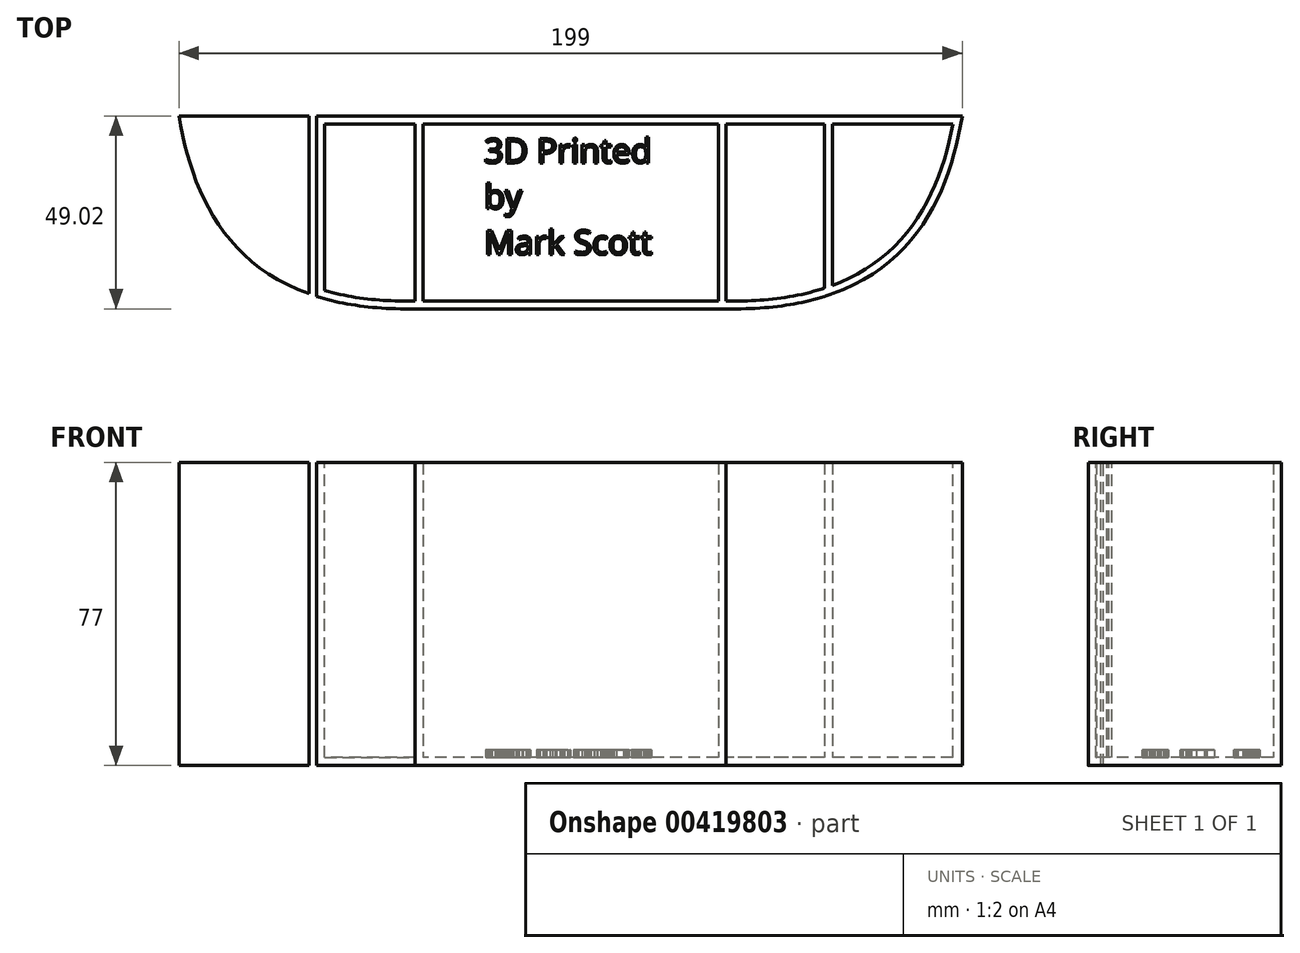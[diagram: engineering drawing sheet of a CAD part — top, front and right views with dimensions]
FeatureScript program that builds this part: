
annotation { "Feature Type Name" : "Feature", "Feature Type Description" : "" }
export const myFeature = defineFeature(function(context is Context, id is Id, definition is map)
    precondition{}
    {
        {
            var Q0;
            Q0=qCreatedBy(makeId("Top.planeOp"),FACE);
            var sketch = newSketch(context, id + "F0", { "sketchPlane" : qUnion([Q0])});
            skLineSegment(sketch, "E0.bottom", {"start": v(37.5, 22.5) * mm, "end": v(-37.5, 22.5) * mm});
            skLineSegment(sketch, "E0.top", {"start": v(37.5, -22.5) * mm, "end": v(-37.5, -22.5) * mm});
            skLineSegment(sketch, "E0.left", {"start": v(37.5, 22.5) * mm, "end": v(37.5, -22.5) * mm});
            skLineSegment(sketch, "E0.right", {"start": v(-37.5, 22.5) * mm, "end": v(-37.5, -22.5) * mm});
            skPoint(sketch, "E0.middle", {"position": v(0, 0) * mm});
            skLineSegment(sketch, "E1.bottom", {"start": v(39.5, -24.5) * mm, "end": v(-39.5, -24.5) * mm});
            skLineSegment(sketch, "E1.top", {"start": v(39.5, 24.5) * mm, "end": v(-39.5, 24.5) * mm});
            skLineSegment(sketch, "E1.left", {"start": v(39.5, -24.5) * mm, "end": v(39.5, 24.5) * mm});
            skLineSegment(sketch, "E1.right", {"start": v(-39.5, -24.5) * mm, "end": v(-39.5, 24.5) * mm});
            skSolve(sketch);
        }
        {
            var Q0;
            Q0=makeQuery(id+"F0.imprint","IMPRINT",FACE,{"disambiguationData":[TD([[makeQuery(id+"F0.imprint","IMPRINT",EDGE,{"derivedFrom":sQuery(id+"F0.wireOp",EDGE,"E0.bottom")}),-1.0]])]});
            var Q1;
            Q1=makeQuery(id+"F0.imprint","IMPRINT",FACE,{"disambiguationData":[TD([[makeQuery(id+"F0.imprint","IMPRINT",EDGE,{"derivedFrom":sQuery(id+"F0.wireOp",EDGE,"E0.bottom")}),1.0]])]});
            extrude(context, id + "F1", {"entities" : qUnion([Q0, Q1]), "oppositeDirection" : true, "depth" : 2 * mm});
        }
        {
            var Q0;
            Q0=makeQuery(id+"F0.imprint","IMPRINT",FACE,{"disambiguationData":[TD([[makeQuery(id+"F0.imprint","IMPRINT",EDGE,{"derivedFrom":sQuery(id+"F0.wireOp",EDGE,"E0.bottom")}),-1.0]])]});
            extrude(context, id + "F2", {"entities" : qUnion([Q0]), "operationType" : NewBodyOperationType.ADD, "depth" : 75 * mm});
        }
        {
            var Q0;
            Q0=qCreatedBy(makeId("Top.planeOp"),FACE);
            var sketch = newSketch(context, id + "F3", { "sketchPlane" : qUnion([Q0])});
            skLineSegment(sketch, "E2", {"start": v(-39.5, 24.5) * mm, "end": v(-99.5, 24.5) * mm});
            skLineSegment(sketch, "E3", {"start": v(-39.5, -24.5) * mm, "end": v(-39.5, 24.5) * mm});
            skFitSpline(sketch, "E4", {"points": [v(-99.5, 24.5) * mm, v(-39.5, -24.5) * mm], "startDerivative": vector(12.26, -73.5) * mm, "endDerivative": vector(130.1, 2.37) * mm});
            skLineSegment(sketch, "E5.bottom", {"start": v(-66.5, 24.5) * mm, "end": v(-64.5, 24.5) * mm});
            skLineSegment(sketch, "E5.left", {"start": v(-66.5, 24.5) * mm, "end": v(-66.5, -20.66) * mm});
            skLineSegment(sketch, "E5.right", {"start": v(-64.5, 24.5) * mm, "end": v(-64.5, -21.33) * mm});
            skLineSegment(sketch, "E6.MirrorCS", {"start": v(66.5, 24.5) * mm, "end": v(64.5, 24.5) * mm});
            skLineSegment(sketch, "E7.MirrorCS", {"start": v(39.5, -24.5) * mm, "end": v(39.5, 24.5) * mm});
            skLineSegment(sketch, "E8.MirrorCS", {"start": v(39.5, 24.5) * mm, "end": v(99.5, 24.5) * mm});
            skLineSegment(sketch, "E9.MirrorCS", {"start": v(66.5, 24.5) * mm, "end": v(66.5, -20.66) * mm});
            skLineSegment(sketch, "E10.MirrorCS", {"start": v(64.5, 24.5) * mm, "end": v(64.5, -21.33) * mm});
            skFitSpline(sketch, "E11.MirrorCS", {"points": [v(99.5, 24.5) * mm, v(39.5, -24.5) * mm], "startDerivative": vector(-12.26, -73.5) * mm, "endDerivative": vector(-130.1, 2.37) * mm});
            skSolve(sketch);
        }
        {
            var Q0;
            {var subQ3=sQuery(id+"F3.wireOp",EDGE,"E5.left");Q0=makeQuery(id+"F3.imprint","IMPRINT",FACE,{"disambiguationData":[TD([[makeQuery(id+"F3.imprint","IMPRINT",EDGE,{"derivedFrom":subQ3}),-1.0]])]});}
            var Q1;
            {var subQ0=sQuery(id+"F3.wireOp",EDGE,"E3");Q1=makeQuery(id+"F3.imprint","IMPRINT",FACE,{"disambiguationData":[TD([[makeQuery(id+"F3.imprint","IMPRINT",EDGE,{"derivedFrom":subQ0}),1.0]])]});}
            var Q2;
            Q2=makeQuery(id+"F3.imprint","IMPRINT",FACE,{"disambiguationData":[TD([[makeQuery(id+"F3.imprint","IMPRINT",EDGE,{"derivedFrom":sQuery(id+"F3.wireOp",EDGE,"E5.bottom")}),-1.0]])]});
            var Q3;
            {var subQ0=sQuery(id+"F3.wireOp",EDGE,"E7.MirrorCS");Q3=makeQuery(id+"F3.imprint","IMPRINT",FACE,{"disambiguationData":[TD([[makeQuery(id+"F3.imprint","IMPRINT",EDGE,{"derivedFrom":subQ0}),-1.0]])]});}
            var Q4;
            {var subQ0=sQuery(id+"F3.wireOp",EDGE,"E9.MirrorCS");Q4=makeQuery(id+"F3.imprint","IMPRINT",FACE,{"disambiguationData":[TD([[makeQuery(id+"F3.imprint","IMPRINT",EDGE,{"derivedFrom":subQ0}),-1.0]])]});}
            var Q5;
            {var subQ3=sQuery(id+"F3.wireOp",EDGE,"E9.MirrorCS");Q5=makeQuery(id+"F3.imprint","IMPRINT",FACE,{"disambiguationData":[TD([[makeQuery(id+"F3.imprint","IMPRINT",EDGE,{"derivedFrom":subQ3}),1.0]])]});}
            extrude(context, id + "F4", {"entities" : qUnion([Q0, Q1, Q2, Q3, Q4, Q5]), "operationType" : NewBodyOperationType.ADD, "oppositeDirection" : true, "depth" : 2 * mm});
        }
        {
            var Q0;
            {var subQ3=sQuery(id+"F3.wireOp",EDGE,"E5.left");Q0=makeQuery(id+"F3.imprint","IMPRINT",FACE,{"disambiguationData":[TD([[makeQuery(id+"F3.imprint","IMPRINT",EDGE,{"derivedFrom":subQ3}),-1.0]])]});}
            var Q1;
            Q1=makeQuery(id+"F3.imprint","IMPRINT",FACE,{"disambiguationData":[TD([[makeQuery(id+"F3.imprint","IMPRINT",EDGE,{"derivedFrom":sQuery(id+"F3.wireOp",EDGE,"E5.bottom")}),-1.0]])]});
            var Q2;
            {var subQ0=sQuery(id+"F3.wireOp",EDGE,"E3");Q2=makeQuery(id+"F3.imprint","IMPRINT",FACE,{"disambiguationData":[TD([[makeQuery(id+"F3.imprint","IMPRINT",EDGE,{"derivedFrom":subQ0}),1.0]])]});}
            var Q3;
            {var subQ0=sQuery(id+"F3.wireOp",EDGE,"E7.MirrorCS");Q3=makeQuery(id+"F3.imprint","IMPRINT",FACE,{"disambiguationData":[TD([[makeQuery(id+"F3.imprint","IMPRINT",EDGE,{"derivedFrom":subQ0}),-1.0]])]});}
            var Q4;
            {var subQ0=sQuery(id+"F3.wireOp",EDGE,"E9.MirrorCS");Q4=makeQuery(id+"F3.imprint","IMPRINT",FACE,{"disambiguationData":[TD([[makeQuery(id+"F3.imprint","IMPRINT",EDGE,{"derivedFrom":subQ0}),-1.0]])]});}
            var Q5;
            {var subQ3=sQuery(id+"F3.wireOp",EDGE,"E9.MirrorCS");Q5=makeQuery(id+"F3.imprint","IMPRINT",FACE,{"disambiguationData":[TD([[makeQuery(id+"F3.imprint","IMPRINT",EDGE,{"derivedFrom":subQ3}),1.0]])]});}
            var Q6;
            Q6=makeQuery(id+"F2.opExtrude","CAP_FACE",FACE,{"disambiguationData":[OSD([sQuery(id+"F0.wireOp",EDGE,"E0.bottom"),sQuery(id+"F0.wireOp",EDGE,"E0.top"),sQuery(id+"F0.wireOp",EDGE,"E0.left"),sQuery(id+"F0.wireOp",EDGE,"E0.right"),sQuery(id+"F0.wireOp",EDGE,"E1.bottom"),sQuery(id+"F0.wireOp",EDGE,"E1.top"),sQuery(id+"F0.wireOp",EDGE,"E1.left"),sQuery(id+"F0.wireOp",EDGE,"E1.right")])],"isStart":false});
            extrude(context, id + "F5", {"entities" : qUnion([Q0, Q1, Q2, Q3, Q4, Q5]), "operationType" : NewBodyOperationType.ADD, "endBound" : BoundingType.UP_TO_SURFACE, "endBoundEntityFace" : qUnion([Q6]), "depth" : 25 * mm});
        }
        {
            var Q0;
            {var subQ0=sQuery(id+"F0.wireOp",EDGE,"E1.right");var subQ1=sQuery(id+"F0.wireOp",EDGE,"E1.left");var subQ2=sQuery(id+"F0.wireOp",EDGE,"E1.top");var subQ3=sQuery(id+"F0.wireOp",EDGE,"E1.bottom");var subQ4=sQuery(id+"F0.wireOp",EDGE,"E0.right");var subQ5=sQuery(id+"F0.wireOp",EDGE,"E0.left");var subQ6=sQuery(id+"F0.wireOp",EDGE,"E0.top");var subQ7=sQuery(id+"F0.wireOp",EDGE,"E0.bottom");Q0=makeQuery(id+"F5.boolean.opBoolean","MERGE",FACE,{"derivedFrom":[makeQuery(id+"F2.opExtrude","CAP_FACE",FACE,{"disambiguationData":[OSD([subQ7,subQ6,subQ5,subQ4,subQ3,subQ2,subQ1,subQ0])],"isStart":false}),makeQuery(id+"F5.opExtrude","CAP_FACE",FACE,{"disambiguationData":[OSD([subQ7,subQ6,subQ5,subQ4,subQ3,subQ2,subQ1,subQ0])],"isStart":false})]});}
            shell(context, id + "F6", {"entities" : qUnion([Q0]), "thickness" : 2 * mm});
        }
        {
            var Q0;
            Q0=makeQuery(id+"F3.imprint","IMPRINT",FACE,{"disambiguationData":[TD([[makeQuery(id+"F3.imprint","IMPRINT",EDGE,{"derivedFrom":sQuery(id+"F3.wireOp",EDGE,"E5.bottom")}),-1.0]])]});
            var Q1;
            {var subQ0=sQuery(id+"F3.wireOp",EDGE,"E9.MirrorCS");Q1=makeQuery(id+"F3.imprint","IMPRINT",FACE,{"disambiguationData":[TD([[makeQuery(id+"F3.imprint","IMPRINT",EDGE,{"derivedFrom":subQ0}),-1.0]])]});}
            var Q2;
            {var subQ0=sQuery(id+"F0.wireOp",EDGE,"E1.right");var subQ1=sQuery(id+"F0.wireOp",EDGE,"E1.left");var subQ2=sQuery(id+"F0.wireOp",EDGE,"E1.top");var subQ3=sQuery(id+"F0.wireOp",EDGE,"E1.bottom");var subQ4=sQuery(id+"F0.wireOp",EDGE,"E0.right");var subQ5=sQuery(id+"F0.wireOp",EDGE,"E0.left");var subQ6=sQuery(id+"F0.wireOp",EDGE,"E0.top");var subQ7=sQuery(id+"F0.wireOp",EDGE,"E0.bottom");var subQ8=sQuery(id+"F3.wireOp",EDGE,"E2");Q2=makeQuery(id+"F5.boolean.opBoolean","MERGE",FACE,{"derivedFrom":[makeQuery(id+"F2.opExtrude","CAP_FACE",FACE,{"disambiguationData":[OSD([subQ7,subQ6,subQ5,subQ4,subQ3,subQ2,subQ1,subQ0])],"isStart":false}),makeQuery(id+"F5.opExtrude","CAP_FACE",FACE,{"disambiguationData":[OSD([subQ7,subQ6,subQ5,subQ4,subQ3,subQ2,subQ1,subQ0]),ownerDisambiguation([makeQuery(id+"F3.imprint","IMPRINT",EDGE,{"disambiguationData":[TD([[makeQuery(id+"F3.imprint","INTERSECT",VERTEX,{"derivedFrom":[subQ8,sQuery(id+"F3.wireOp",EDGE,"E3")]}),-1.0]])],"derivedFrom":subQ8})])],"isStart":false}),makeQuery(id+"F5.opExtrude","CAP_FACE",FACE,{"disambiguationData":[OSD([subQ7,subQ6,subQ5,subQ4,subQ3,subQ2,subQ1,subQ0]),ownerDisambiguation([makeQuery(id+"F3.imprint","IMPRINT",EDGE,{"derivedFrom":sQuery(id+"F3.wireOp",EDGE,"E7.MirrorCS")})])],"isStart":false})]});}
            extrude(context, id + "F7", {"entities" : qUnion([Q0, Q1]), "operationType" : NewBodyOperationType.ADD, "endBound" : BoundingType.UP_TO_SURFACE, "endBoundEntityFace" : qUnion([Q2]), "depth" : 25 * mm});
        }
        {
            var Q0;
            Q0=makeQuery(id+"F1.opExtrude","CAP_FACE",FACE,{"disambiguationData":[OSD([sQuery(id+"F0.wireOp",EDGE,"E1.bottom"),sQuery(id+"F0.wireOp",EDGE,"E1.top"),sQuery(id+"F0.wireOp",EDGE,"E1.left"),sQuery(id+"F0.wireOp",EDGE,"E1.right")])],"isStart":true});
            var sketch = newSketch(context, id + "F8", { "sketchPlane" : qUnion([Q0])});
            skText(sketch, "E12", { "text": "3D Printed\nby \nMark Scott", "fontName": "OpenSans-Regular.ttf"});
            const initialGuessF8  = {"E12": [-0.02195, 0.0126, 1, 0, 0.00616]};
            skSetInitialGuess(sketch, initialGuessF8);
            skSolve(sketch);
        }
        {
            var Q0;
            Q0 = qSketchRegion(id + "F8", true);
            extrude(context, id + "F9", {"entities" : qUnion([Q0]), "operationType" : NewBodyOperationType.ADD, "depth" : 2 * mm});
        }
    });
